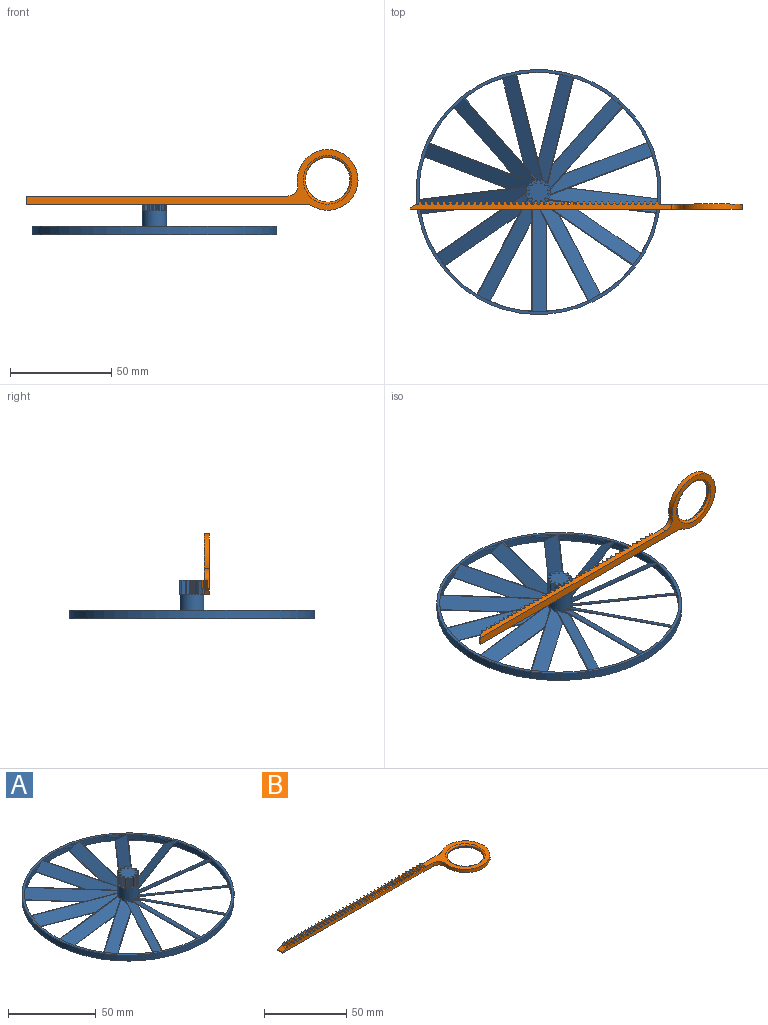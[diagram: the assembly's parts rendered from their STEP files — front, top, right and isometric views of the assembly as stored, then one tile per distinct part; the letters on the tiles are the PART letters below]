
ASSEMBLY  parts=2 mates=1
PART A: 95 faces, bbox 121.1x121.1x19.1 mm
  f0: plane 2.1x1.71mm, normal (0,0,1), area 2.1mm2, adj f12,f59,f62,f93
  f1: plane 1.96x1.96mm, normal (0,0,1), area 2.1mm2, adj f12,f90,f92,f94
  f2: plane 2.1x1.71mm, normal (0,0,1), area 2.1mm2, adj f12,f87,f89,f91
  f3: plane 2.1x1.71mm, normal (0,0,1), area 2.1mm2, adj f12,f84,f86,f88
  f4: plane 1.96x1.96mm, normal (0,0,1), area 2.1mm2, adj f12,f81,f83,f85
  f5: plane 2.1x1.71mm, normal (0,0,1), area 2.1mm2, adj f12,f78,f80,f82
  f6: plane 2.1x1.71mm, normal (0,0,1), area 2.1mm2, adj f12,f75,f77,f79
  f7: plane 1.96x1.96mm, normal (0,0,1), area 2.1mm2, adj f12,f72,f74,f76
  f8: plane 2.1x1.71mm, normal (0,0,1), area 2.1mm2, adj f12,f69,f71,f73
  f9: plane 2.1x1.71mm, normal (0,0,1), area 2.1mm2, adj f12,f66,f68,f70
  f10: plane 1.96x1.96mm, normal (0,0,1), area 2.1mm2, adj f12,f63,f65,f67
  f11: plane 2.1x1.71mm, normal (0,0,1), area 2.1mm2, adj f12,f58,f61,f64
  f12: cylinder r=6mm len=19mm, axis (0,0,-1), area 474.6mm2, adj f0,f1,f2,f3,f4,f5,f6,f7
  f13: cylinder r=6mm len=1.57mm, axis (0,0,-1), area 0.4mm2, adj f12,f16,f36
  f14: cylinder r=6mm len=4.1mm, axis (0,0,-1), area 2.9mm2, adj f12,f16,f37,f38
  f15: cylinder r=6mm len=5.7mm, axis (0,0,-1), area 6.2mm2, adj f12,f16,f39,f40
  f16: plane 121x121mm, normal (0,0,-1), area 885.8mm2, adj f12,f13,f14,f15,f17,f18,f19,f20
  f17: cylinder r=20mm len=54.2mm, axis (0,1,0), area 430.3mm2, adj f12,f16,f43,f57
  f18: plane 54.47x6.93mm, normal (0.5,0,0.87), area 427.4mm2, adj f12,f16,f44,f57
  f19: cylinder r=20mm len=51.21mm, axis (-0.46,0.89,0), area 430.3mm2, adj f12,f16,f44,f57
  f20: plane 50.9x31.41mm, normal (0.44,-0.23,0.87), area 427.4mm2, adj f12,f16,f43,f57
  f21: plane 51.38x31.16mm, normal (0.44,0.23,0.87), area 427.4mm2, adj f12,f16,f45,f57
  f22: cylinder r=20mm len=48.54mm, axis (-0.82,0.57,0), area 430.3mm2, adj f12,f16,f45,f57
  f23: plane 48.25x36.6mm, normal (0.28,0.41,0.87), area 427.4mm2, adj f12,f16,f46,f57
  f24: cylinder r=20mm len=54.64mm, axis (-0.99,0.12,0), area 430.3mm2, adj f12,f16,f46,f57
  f25: plane 54.29x13.43mm, normal (0.06,0.5,0.87), area 427.4mm2, adj f12,f16,f47,f57
  f26: cylinder r=20mm len=53.14mm, axis (-0.94,-0.35,0), area 430.3mm2, adj f12,f16,f47,f57
  f27: plane 53.31x25.57mm, normal (-0.18,0.47,0.87), area 427.4mm2, adj f12,f16,f48,f57
  f28: cylinder r=20mm len=45.16mm, axis (-0.66,-0.75,0), area 430.3mm2, adj f12,f16,f48,f57
  f29: plane 44.9x41.25mm, normal (-0.37,0.33,0.87), area 427.4mm2, adj f12,f16,f49,f57
  f30: cylinder r=20mm len=54.28mm, axis (-0.24,-0.97,0), area 430.3mm2, adj f12,f16,f49,f57
  f31: plane 53.94x19.74mm, normal (-0.49,0.12,0.87), area 427.4mm2, adj f12,f16,f50,f57
  f32: cylinder r=20mm len=54.28mm, axis (0.24,-0.97,0), area 430.3mm2, adj f12,f16,f50,f57
  f33: plane 54.47x19.61mm, normal (-0.49,-0.12,0.87), area 427.4mm2, adj f12,f16,f51,f57
  f34: cylinder r=20mm len=45.16mm, axis (0.66,-0.75,0), area 430.3mm2, adj f12,f16,f51,f57
  f35: plane 45.3x40.9mm, normal (-0.37,-0.33,0.87), area 427.4mm2, adj f12,f16,f52,f57
  f36: cylinder r=20mm len=53.14mm, axis (0.94,-0.35,0), area 430.3mm2, adj f12,f13,f16,f52,f57
  f37: plane 52.9x25.85mm, normal (-0.18,-0.47,0.87), area 427.4mm2, adj f12,f14,f16,f53,f57
  f38: cylinder r=20mm len=54.64mm, axis (0.99,0.12,0), area 430.3mm2, adj f12,f14,f16,f53,f57
  f39: plane 54.87x13.42mm, normal (0.06,-0.5,0.87), area 427.4mm2, adj f12,f15,f16,f54,f57
  f40: cylinder r=20mm len=48.54mm, axis (0.82,0.57,0), area 430.3mm2, adj f15,f16,f54,f57
  f41: plane 48.7x36.29mm, normal (0.28,-0.41,0.87), area 427.4mm2, adj f12,f16,f55,f57
  f42: cylinder r=20mm len=51.21mm, axis (0.46,0.89,0), area 430.3mm2, adj f12,f16,f55,f57
  f43: cylinder r=59.1mm len=33.65mm, axis (0,0,-1), area 110.7mm2, adj f16,f17,f20,f57
  f44: cylinder r=59.1mm len=33.6mm, axis (0,0,-1), area 110.7mm2, adj f16,f18,f19,f57
  f45: cylinder r=59.1mm len=25.85mm, axis (0,0,-1), area 110.7mm2, adj f16,f21,f22,f57
  f46: cylinder r=59.1mm len=32.42mm, axis (0,0,-1), area 110.7mm2, adj f16,f23,f24,f57
  f47: cylinder r=59.1mm len=34.37mm, axis (0,0,-1), area 110.7mm2, adj f16,f25,f26,f57
  f48: cylinder r=59.1mm len=28.44mm, axis (0,0,-1), area 110.7mm2, adj f16,f27,f28,f57
  f49: cylinder r=59.1mm len=30.71mm, axis (0,0,-1), area 110.7mm2, adj f16,f29,f30,f57
  f50: cylinder r=59.1mm len=34.63mm, axis (0,0,-1), area 110.7mm2, adj f16,f31,f32,f57
  f51: cylinder r=59.1mm len=30.62mm, axis (0,0,-1), area 110.7mm2, adj f16,f33,f34,f57
  f52: cylinder r=59.1mm len=28.56mm, axis (0,0,-1), area 110.7mm2, adj f16,f35,f36,f57
  f53: cylinder r=59.1mm len=34.39mm, axis (0,0,-1), area 110.7mm2, adj f16,f37,f38,f57
  f54: cylinder r=59.1mm len=32.34mm, axis (0,0,-1), area 110.7mm2, adj f16,f39,f40,f57
  f55: cylinder r=59.1mm len=25.99mm, axis (0,0,-1), area 110.7mm2, adj f16,f41,f42,f57
  f56: cylinder r=60.5mm len=121mm, axis (0,0,-1), area 1520.5mm2, adj f16,f57
  f57: plane 121x121mm, normal (0,0,1), area 771.7mm2, adj f12,f17,f18,f19,f20,f21,f22,f23
  f58: plane 7x1.57mm, normal (-0.97,0.26,0), area 11.4mm2, adj f11,f12,f60,f61
  f59: plane 7x1.57mm, normal (0.97,0.26,0), area 11.4mm2, adj f0,f12,f60,f62
  f60: plane 12x12mm, normal (0,0,1), area 88.4mm2, adj f12,f58,f59,f61,f62,f63,f64,f65
  f61: cylinder r=4.5mm len=7mm, axis (0,0,-1), area 3.8mm2, adj f11,f58,f60,f64
  f62: cylinder r=4.5mm len=7mm, axis (0,0,-1), area 3.8mm2, adj f0,f59,f60,f93
  f63: plane 7x1.57mm, normal (-0.97,-0.26,0), area 11.4mm2, adj f10,f12,f60,f65
  f64: plane 7x1.15mm, normal (0.71,0.71,0), area 11.4mm2, adj f11,f12,f60,f61
  f65: cylinder r=4.5mm len=7mm, axis (0,0,-1), area 3.8mm2, adj f10,f60,f63,f67
  f66: plane 7x1.15mm, normal (-0.71,-0.71,0), area 11.4mm2, adj f9,f12,f60,f68
  f67: plane 7x1.57mm, normal (0.26,0.97,0), area 11.4mm2, adj f10,f12,f60,f65
  f68: cylinder r=4.5mm len=7mm, axis (0,0,-1), area 3.8mm2, adj f9,f60,f66,f70
  f69: plane 7x1.57mm, normal (-0.26,-0.97,0), area 11.4mm2, adj f8,f12,f60,f71
  f70: plane 7x1.57mm, normal (-0.26,0.97,0), area 11.4mm2, adj f9,f12,f60,f68
  f71: cylinder r=4.5mm len=7mm, axis (0,0,-1), area 3.8mm2, adj f8,f60,f69,f73
  f72: plane 7x1.57mm, normal (0.26,-0.97,0), area 11.4mm2, adj f7,f12,f60,f74
  f73: plane 7x1.15mm, normal (-0.71,0.71,0), area 11.4mm2, adj f8,f12,f60,f71
  f74: cylinder r=4.5mm len=7mm, axis (0,0,-1), area 3.8mm2, adj f7,f60,f72,f76
  f75: plane 7x1.15mm, normal (0.71,-0.71,0), area 11.4mm2, adj f6,f12,f60,f77
  f76: plane 7x1.57mm, normal (-0.97,0.26,0), area 11.4mm2, adj f7,f12,f60,f74
  f77: cylinder r=4.5mm len=7mm, axis (0,0,-1), area 3.8mm2, adj f6,f60,f75,f79
  f78: plane 7x1.57mm, normal (0.97,-0.26,0), area 11.4mm2, adj f5,f12,f60,f80
  f79: plane 7x1.57mm, normal (-0.97,-0.26,0), area 11.4mm2, adj f6,f12,f60,f77
  f80: cylinder r=4.5mm len=7mm, axis (0,0,-1), area 3.8mm2, adj f5,f60,f78,f82
  f81: plane 7x1.57mm, normal (0.97,0.26,0), area 11.4mm2, adj f4,f12,f60,f83
  f82: plane 7x1.15mm, normal (-0.71,-0.71,0), area 11.4mm2, adj f5,f12,f60,f80
  f83: cylinder r=4.5mm len=7mm, axis (0,0,-1), area 3.8mm2, adj f4,f60,f81,f85
  f84: plane 7x1.15mm, normal (0.71,0.71,0), area 11.4mm2, adj f3,f12,f60,f86
  f85: plane 7x1.57mm, normal (-0.26,-0.97,0), area 11.4mm2, adj f4,f12,f60,f83
  f86: cylinder r=4.5mm len=7mm, axis (0,0,-1), area 3.8mm2, adj f3,f60,f84,f88
  f87: plane 7x1.57mm, normal (0.26,0.97,0), area 11.4mm2, adj f2,f12,f60,f89
  f88: plane 7x1.57mm, normal (0.26,-0.97,0), area 11.4mm2, adj f3,f12,f60,f86
  f89: cylinder r=4.5mm len=7mm, axis (0,0,-1), area 3.8mm2, adj f2,f60,f87,f91
  f90: plane 7x1.57mm, normal (-0.26,0.97,0), area 11.4mm2, adj f1,f12,f60,f92
  f91: plane 7x1.15mm, normal (0.71,-0.71,0), area 11.4mm2, adj f2,f12,f60,f89
  f92: cylinder r=4.5mm len=7mm, axis (0,0,-1), area 3.8mm2, adj f1,f60,f90,f94
  f93: plane 7x1.15mm, normal (-0.71,0.71,0), area 11.4mm2, adj f0,f12,f60,f62
  f94: plane 7x1.57mm, normal (0.97,-0.26,0), area 11.4mm2, adj f1,f12,f60,f92
PART B: 252 faces, bbox 164x30x3.8 mm
  f0: plane 4x0.94mm, normal (-0.87,0,0.49), area 4.3mm2, adj f1,f6,f7,f8
  f1: plane 4x0.38mm, normal (-0.81,0,0.59), area 1.9mm2, adj f0,f7,f8,f243
  f2: plane 164.01x30mm, normal (0,0,-1), area 816.3mm2, adj f7,f8,f245,f246,f248,f250,f251
  f3: plane 4x1mm, normal (0,0,1), area 4mm2, adj f4,f7,f8,f10
  f4: plane 4x0.38mm, normal (0.81,0,0.59), area 1.9mm2, adj f3,f5,f7,f8
  f5: plane 4x0.94mm, normal (0.87,0,0.49), area 4.3mm2, adj f4,f6,f7,f8
  f6: plane 4x0.4mm, normal (0,0,1), area 1.6mm2, adj f0,f5,f7,f8
  f7: plane 129.23x3.82mm, normal (0,-1,0), area 380.9mm2, adj f0,f1,f2,f3,f4,f5,f6,f9
  f8: plane 138.47x3.82mm, normal (0,1,0), area 404mm2, adj f0,f1,f2,f3,f4,f5,f6,f9
  f9: plane 4x0.94mm, normal (-0.87,0,0.49), area 4.3mm2, adj f7,f8,f10,f14
  f10: plane 4x0.38mm, normal (-0.81,0,0.59), area 1.9mm2, adj f3,f7,f8,f9
  f11: plane 4x1mm, normal (0,0,1), area 4mm2, adj f7,f8,f12,f16
  f12: plane 4x0.38mm, normal (0.81,0,0.59), area 1.9mm2, adj f7,f8,f11,f13
  f13: plane 4x0.94mm, normal (0.87,0,0.49), area 4.3mm2, adj f7,f8,f12,f14
  f14: plane 4x0.4mm, normal (0,0,1), area 1.6mm2, adj f7,f8,f9,f13
  f15: plane 4x0.94mm, normal (-0.87,0,0.49), area 4.3mm2, adj f7,f8,f16,f20
  f16: plane 4x0.38mm, normal (-0.81,0,0.59), area 1.9mm2, adj f7,f8,f11,f15
  f17: plane 4x1mm, normal (0,0,1), area 4mm2, adj f7,f8,f18,f22
  f18: plane 4x0.38mm, normal (0.81,0,0.59), area 1.9mm2, adj f7,f8,f17,f19
  f19: plane 4x0.94mm, normal (0.87,0,0.49), area 4.3mm2, adj f7,f8,f18,f20
  f20: plane 4x0.4mm, normal (0,0,1), area 1.6mm2, adj f7,f8,f15,f19
  f21: plane 4x0.94mm, normal (-0.87,0,0.49), area 4.3mm2, adj f7,f8,f22,f26
  f22: plane 4x0.38mm, normal (-0.81,0,0.59), area 1.9mm2, adj f7,f8,f17,f21
  f23: plane 4x1mm, normal (0,0,1), area 4mm2, adj f7,f8,f24,f28
  f24: plane 4x0.38mm, normal (0.81,0,0.59), area 1.9mm2, adj f7,f8,f23,f25
  f25: plane 4x0.94mm, normal (0.87,0,0.49), area 4.3mm2, adj f7,f8,f24,f26
  f26: plane 4x0.4mm, normal (0,0,1), area 1.6mm2, adj f7,f8,f21,f25
  f27: plane 4x0.94mm, normal (-0.87,0,0.49), area 4.3mm2, adj f7,f8,f28,f32
  f28: plane 4x0.38mm, normal (-0.81,0,0.59), area 1.9mm2, adj f7,f8,f23,f27
  f29: plane 4x1mm, normal (0,0,1), area 4mm2, adj f7,f8,f30,f34
  f30: plane 4x0.38mm, normal (0.81,0,0.59), area 1.9mm2, adj f7,f8,f29,f31
  f31: plane 4x0.94mm, normal (0.87,0,0.49), area 4.3mm2, adj f7,f8,f30,f32
  f32: plane 4x0.4mm, normal (0,0,1), area 1.6mm2, adj f7,f8,f27,f31
  f33: plane 4x0.94mm, normal (-0.87,0,0.49), area 4.3mm2, adj f7,f8,f34,f38
  f34: plane 4x0.38mm, normal (-0.81,0,0.59), area 1.9mm2, adj f7,f8,f29,f33
  f35: plane 4x1mm, normal (0,0,1), area 4mm2, adj f7,f8,f36,f40
  f36: plane 4x0.38mm, normal (0.81,0,0.59), area 1.9mm2, adj f7,f8,f35,f37
  f37: plane 4x0.94mm, normal (0.87,0,0.49), area 4.3mm2, adj f7,f8,f36,f38
  f38: plane 4x0.4mm, normal (0,0,1), area 1.6mm2, adj f7,f8,f33,f37
  f39: plane 4x0.94mm, normal (-0.87,0,0.49), area 4.3mm2, adj f7,f8,f40,f44
  f40: plane 4x0.38mm, normal (-0.81,0,0.59), area 1.9mm2, adj f7,f8,f35,f39
  f41: plane 4x1mm, normal (0,0,1), area 4mm2, adj f7,f8,f42,f46
  f42: plane 4x0.38mm, normal (0.81,0,0.59), area 1.9mm2, adj f7,f8,f41,f43
  f43: plane 4x0.94mm, normal (0.87,0,0.49), area 4.3mm2, adj f7,f8,f42,f44
  f44: plane 4x0.4mm, normal (0,0,1), area 1.6mm2, adj f7,f8,f39,f43
  f45: plane 4x0.94mm, normal (-0.87,0,0.49), area 4.3mm2, adj f7,f8,f46,f50
  f46: plane 4x0.38mm, normal (-0.81,0,0.59), area 1.9mm2, adj f7,f8,f41,f45
  f47: plane 4x1mm, normal (0,0,1), area 4mm2, adj f7,f8,f48,f52
  f48: plane 4x0.38mm, normal (0.81,0,0.59), area 1.9mm2, adj f7,f8,f47,f49
  f49: plane 4x0.94mm, normal (0.87,0,0.49), area 4.3mm2, adj f7,f8,f48,f50
  f50: plane 4x0.4mm, normal (0,0,1), area 1.6mm2, adj f7,f8,f45,f49
  f51: plane 4x0.94mm, normal (-0.87,0,0.49), area 4.3mm2, adj f7,f8,f52,f56
  f52: plane 4x0.38mm, normal (-0.81,0,0.59), area 1.9mm2, adj f7,f8,f47,f51
  f53: plane 4x1mm, normal (0,0,1), area 4mm2, adj f7,f8,f54,f58
  f54: plane 4x0.38mm, normal (0.81,0,0.59), area 1.9mm2, adj f7,f8,f53,f55
  f55: plane 4x0.94mm, normal (0.87,0,0.49), area 4.3mm2, adj f7,f8,f54,f56
  f56: plane 4x0.4mm, normal (0,0,1), area 1.6mm2, adj f7,f8,f51,f55
  f57: plane 4x0.94mm, normal (-0.87,0,0.49), area 4.3mm2, adj f7,f8,f58,f62
  f58: plane 4x0.38mm, normal (-0.81,0,0.59), area 1.9mm2, adj f7,f8,f53,f57
  f59: plane 4x1mm, normal (0,0,1), area 4mm2, adj f7,f8,f60,f64
  f60: plane 4x0.38mm, normal (0.81,0,0.59), area 1.9mm2, adj f7,f8,f59,f61
  f61: plane 4x0.94mm, normal (0.87,0,0.49), area 4.3mm2, adj f7,f8,f60,f62
  f62: plane 4x0.4mm, normal (0,0,1), area 1.6mm2, adj f7,f8,f57,f61
  f63: plane 4x0.94mm, normal (-0.87,0,0.49), area 4.3mm2, adj f7,f8,f64,f68
  f64: plane 4x0.38mm, normal (-0.81,0,0.59), area 1.9mm2, adj f7,f8,f59,f63
  f65: plane 4x1mm, normal (0,0,1), area 4mm2, adj f7,f8,f66,f70
  f66: plane 4x0.38mm, normal (0.81,0,0.59), area 1.9mm2, adj f7,f8,f65,f67
  f67: plane 4x0.94mm, normal (0.87,0,0.49), area 4.3mm2, adj f7,f8,f66,f68
  f68: plane 4x0.4mm, normal (0,0,1), area 1.6mm2, adj f7,f8,f63,f67
  f69: plane 4x0.94mm, normal (-0.87,0,0.49), area 4.3mm2, adj f7,f8,f70,f74
  f70: plane 4x0.38mm, normal (-0.81,0,0.59), area 1.9mm2, adj f7,f8,f65,f69
  f71: plane 4x1mm, normal (0,0,1), area 4mm2, adj f7,f8,f72,f76
  f72: plane 4x0.38mm, normal (0.81,0,0.59), area 1.9mm2, adj f7,f8,f71,f73
  f73: plane 4x0.94mm, normal (0.87,0,0.49), area 4.3mm2, adj f7,f8,f72,f74
  f74: plane 4x0.4mm, normal (0,0,1), area 1.6mm2, adj f7,f8,f69,f73
  f75: plane 4x0.94mm, normal (-0.87,0,0.49), area 4.3mm2, adj f7,f8,f76,f80
  f76: plane 4x0.38mm, normal (-0.81,0,0.59), area 1.9mm2, adj f7,f8,f71,f75
  f77: plane 4x1mm, normal (0,0,1), area 4mm2, adj f7,f8,f78,f82
  f78: plane 4x0.38mm, normal (0.81,0,0.59), area 1.9mm2, adj f7,f8,f77,f79
  f79: plane 4x0.94mm, normal (0.87,0,0.49), area 4.3mm2, adj f7,f8,f78,f80
  f80: plane 4x0.4mm, normal (0,0,1), area 1.6mm2, adj f7,f8,f75,f79
  f81: plane 4x0.94mm, normal (-0.87,0,0.49), area 4.3mm2, adj f7,f8,f82,f86
  f82: plane 4x0.38mm, normal (-0.81,0,0.59), area 1.9mm2, adj f7,f8,f77,f81
  f83: plane 4x1mm, normal (0,0,1), area 4mm2, adj f7,f8,f84,f88
  f84: plane 4x0.38mm, normal (0.81,0,0.59), area 1.9mm2, adj f7,f8,f83,f85
  f85: plane 4x0.94mm, normal (0.87,0,0.49), area 4.3mm2, adj f7,f8,f84,f86
  f86: plane 4x0.4mm, normal (0,0,1), area 1.6mm2, adj f7,f8,f81,f85
  f87: plane 4x0.94mm, normal (-0.87,0,0.49), area 4.3mm2, adj f7,f8,f88,f92
  f88: plane 4x0.38mm, normal (-0.81,0,0.59), area 1.9mm2, adj f7,f8,f83,f87
  f89: plane 4x1mm, normal (0,0,1), area 4mm2, adj f7,f8,f90,f94
  f90: plane 4x0.38mm, normal (0.81,0,0.59), area 1.9mm2, adj f7,f8,f89,f91
  f91: plane 4x0.94mm, normal (0.87,0,0.49), area 4.3mm2, adj f7,f8,f90,f92
  f92: plane 4x0.4mm, normal (0,0,1), area 1.6mm2, adj f7,f8,f87,f91
  f93: plane 4x0.94mm, normal (-0.87,0,0.49), area 4.3mm2, adj f7,f8,f94,f98
  f94: plane 4x0.38mm, normal (-0.81,0,0.59), area 1.9mm2, adj f7,f8,f89,f93
  f95: plane 4x1mm, normal (0,0,1), area 4mm2, adj f7,f8,f96,f100
  f96: plane 4x0.38mm, normal (0.81,0,0.59), area 1.9mm2, adj f7,f8,f95,f97
  f97: plane 4x0.94mm, normal (0.87,0,0.49), area 4.3mm2, adj f7,f8,f96,f98
  f98: plane 4x0.4mm, normal (0,0,1), area 1.6mm2, adj f7,f8,f93,f97
  f99: plane 4x0.94mm, normal (-0.87,0,0.49), area 4.3mm2, adj f7,f8,f100,f104
  f100: plane 4x0.38mm, normal (-0.81,0,0.59), area 1.9mm2, adj f7,f8,f95,f99
  f101: plane 4x1mm, normal (0,0,1), area 4mm2, adj f7,f8,f102,f106
  f102: plane 4x0.38mm, normal (0.81,0,0.59), area 1.9mm2, adj f7,f8,f101,f103
  f103: plane 4x0.94mm, normal (0.87,0,0.49), area 4.3mm2, adj f7,f8,f102,f104
  f104: plane 4x0.4mm, normal (0,0,1), area 1.6mm2, adj f7,f8,f99,f103
  f105: plane 4x0.94mm, normal (-0.87,0,0.49), area 4.3mm2, adj f7,f8,f106,f110
  f106: plane 4x0.38mm, normal (-0.81,0,0.59), area 1.9mm2, adj f7,f8,f101,f105
  f107: plane 4x1mm, normal (0,0,1), area 4mm2, adj f7,f8,f108,f112
  f108: plane 4x0.38mm, normal (0.81,0,0.59), area 1.9mm2, adj f7,f8,f107,f109
  f109: plane 4x0.94mm, normal (0.87,0,0.49), area 4.3mm2, adj f7,f8,f108,f110
  f110: plane 4x0.4mm, normal (0,0,1), area 1.6mm2, adj f7,f8,f105,f109
  f111: plane 4x0.94mm, normal (-0.87,0,0.49), area 4.3mm2, adj f7,f8,f112,f116
  f112: plane 4x0.38mm, normal (-0.81,0,0.59), area 1.9mm2, adj f7,f8,f107,f111
  f113: plane 4x1mm, normal (0,0,1), area 4mm2, adj f7,f8,f114,f118
  f114: plane 4x0.38mm, normal (0.81,0,0.59), area 1.9mm2, adj f7,f8,f113,f115
  f115: plane 4x0.94mm, normal (0.87,0,0.49), area 4.3mm2, adj f7,f8,f114,f116
  f116: plane 4x0.4mm, normal (0,0,1), area 1.6mm2, adj f7,f8,f111,f115
  f117: plane 4x0.94mm, normal (-0.87,0,0.49), area 4.3mm2, adj f7,f8,f118,f122
  f118: plane 4x0.38mm, normal (-0.81,0,0.59), area 1.9mm2, adj f7,f8,f113,f117
  f119: plane 4x1mm, normal (0,0,1), area 4mm2, adj f7,f8,f120,f124
  f120: plane 4x0.38mm, normal (0.81,0,0.59), area 1.9mm2, adj f7,f8,f119,f121
  f121: plane 4x0.94mm, normal (0.87,0,0.49), area 4.3mm2, adj f7,f8,f120,f122
  f122: plane 4x0.4mm, normal (0,0,1), area 1.6mm2, adj f7,f8,f117,f121
  f123: plane 4x0.94mm, normal (-0.87,0,0.49), area 4.3mm2, adj f7,f8,f124,f128
  f124: plane 4x0.38mm, normal (-0.81,0,0.59), area 1.9mm2, adj f7,f8,f119,f123
  f125: plane 4x1mm, normal (0,0,1), area 4mm2, adj f7,f8,f126,f130
  f126: plane 4x0.38mm, normal (0.81,0,0.59), area 1.9mm2, adj f7,f8,f125,f127
  f127: plane 4x0.94mm, normal (0.87,0,0.49), area 4.3mm2, adj f7,f8,f126,f128
  f128: plane 4x0.4mm, normal (0,0,1), area 1.6mm2, adj f7,f8,f123,f127
  f129: plane 4x0.94mm, normal (-0.87,0,0.49), area 4.3mm2, adj f7,f8,f130,f134
  f130: plane 4x0.38mm, normal (-0.81,0,0.59), area 1.9mm2, adj f7,f8,f125,f129
  f131: plane 4x1mm, normal (0,0,1), area 4mm2, adj f7,f8,f132,f136
  f132: plane 4x0.38mm, normal (0.81,0,0.59), area 1.9mm2, adj f7,f8,f131,f133
  f133: plane 4x0.94mm, normal (0.87,0,0.49), area 4.3mm2, adj f7,f8,f132,f134
  f134: plane 4x0.4mm, normal (0,0,1), area 1.6mm2, adj f7,f8,f129,f133
  f135: plane 4x0.94mm, normal (-0.87,0,0.49), area 4.3mm2, adj f7,f8,f136,f140
  f136: plane 4x0.38mm, normal (-0.81,0,0.59), area 1.9mm2, adj f7,f8,f131,f135
  f137: plane 4x1mm, normal (0,0,1), area 4mm2, adj f7,f8,f138,f142
  f138: plane 4x0.38mm, normal (0.81,0,0.59), area 1.9mm2, adj f7,f8,f137,f139
  f139: plane 4x0.94mm, normal (0.87,0,0.49), area 4.3mm2, adj f7,f8,f138,f140
  f140: plane 4x0.4mm, normal (0,0,1), area 1.6mm2, adj f7,f8,f135,f139
  f141: plane 4x0.94mm, normal (-0.87,0,0.49), area 4.3mm2, adj f7,f8,f142,f146
  f142: plane 4x0.38mm, normal (-0.81,0,0.59), area 1.9mm2, adj f7,f8,f137,f141
  f143: plane 4x1mm, normal (0,0,1), area 4mm2, adj f7,f8,f144,f148
  f144: plane 4x0.38mm, normal (0.81,0,0.59), area 1.9mm2, adj f7,f8,f143,f145
  f145: plane 4x0.94mm, normal (0.87,0,0.49), area 4.3mm2, adj f7,f8,f144,f146
  f146: plane 4x0.4mm, normal (0,0,1), area 1.6mm2, adj f7,f8,f141,f145
  f147: plane 4x0.94mm, normal (-0.87,0,0.49), area 4.3mm2, adj f7,f8,f148,f152
  f148: plane 4x0.38mm, normal (-0.81,0,0.59), area 1.9mm2, adj f7,f8,f143,f147
  f149: plane 4x1mm, normal (0,0,1), area 4mm2, adj f7,f8,f150,f154
  f150: plane 4x0.38mm, normal (0.81,0,0.59), area 1.9mm2, adj f7,f8,f149,f151
  f151: plane 4x0.94mm, normal (0.87,0,0.49), area 4.3mm2, adj f7,f8,f150,f152
  f152: plane 4x0.4mm, normal (0,0,1), area 1.6mm2, adj f7,f8,f147,f151
  f153: plane 4x0.94mm, normal (-0.87,0,0.49), area 4.3mm2, adj f7,f8,f154,f158
  f154: plane 4x0.38mm, normal (-0.81,0,0.59), area 1.9mm2, adj f7,f8,f149,f153
  f155: plane 4x1mm, normal (0,0,1), area 4mm2, adj f7,f8,f156,f160
  f156: plane 4x0.38mm, normal (0.81,0,0.59), area 1.9mm2, adj f7,f8,f155,f157
  f157: plane 4x0.94mm, normal (0.87,0,0.49), area 4.3mm2, adj f7,f8,f156,f158
  f158: plane 4x0.4mm, normal (0,0,1), area 1.6mm2, adj f7,f8,f153,f157
  f159: plane 4x0.94mm, normal (-0.87,0,0.49), area 4.3mm2, adj f7,f8,f160,f164
  f160: plane 4x0.38mm, normal (-0.81,0,0.59), area 1.9mm2, adj f7,f8,f155,f159
  f161: plane 4x1mm, normal (0,0,1), area 4mm2, adj f7,f8,f162,f166
  f162: plane 4x0.38mm, normal (0.81,0,0.59), area 1.9mm2, adj f7,f8,f161,f163
  f163: plane 4x0.94mm, normal (0.87,0,0.49), area 4.3mm2, adj f7,f8,f162,f164
  f164: plane 4x0.4mm, normal (0,0,1), area 1.6mm2, adj f7,f8,f159,f163
  f165: plane 4x0.94mm, normal (-0.87,0,0.49), area 4.3mm2, adj f7,f8,f166,f170
  f166: plane 4x0.38mm, normal (-0.81,0,0.59), area 1.9mm2, adj f7,f8,f161,f165
  f167: plane 4x1mm, normal (0,0,1), area 4mm2, adj f7,f8,f168,f172
  f168: plane 4x0.38mm, normal (0.81,0,0.59), area 1.9mm2, adj f7,f8,f167,f169
  f169: plane 4x0.94mm, normal (0.87,0,0.49), area 4.3mm2, adj f7,f8,f168,f170
  f170: plane 4x0.4mm, normal (0,0,1), area 1.6mm2, adj f7,f8,f165,f169
  f171: plane 4x0.94mm, normal (-0.87,0,0.49), area 4.3mm2, adj f7,f8,f172,f176
  f172: plane 4x0.38mm, normal (-0.81,0,0.59), area 1.9mm2, adj f7,f8,f167,f171
  f173: plane 4x1mm, normal (0,0,1), area 4mm2, adj f7,f8,f174,f178
  f174: plane 4x0.38mm, normal (0.81,0,0.59), area 1.9mm2, adj f7,f8,f173,f175
  f175: plane 4x0.94mm, normal (0.87,0,0.49), area 4.3mm2, adj f7,f8,f174,f176
  f176: plane 4x0.4mm, normal (0,0,1), area 1.6mm2, adj f7,f8,f171,f175
  f177: plane 4x0.94mm, normal (-0.87,0,0.49), area 4.3mm2, adj f7,f8,f178,f182
  f178: plane 4x0.38mm, normal (-0.81,0,0.59), area 1.9mm2, adj f7,f8,f173,f177
  f179: plane 4x1mm, normal (0,0,1), area 4mm2, adj f7,f8,f180,f184
  f180: plane 4x0.38mm, normal (0.81,0,0.59), area 1.9mm2, adj f7,f8,f179,f181
  f181: plane 4x0.94mm, normal (0.87,0,0.49), area 4.3mm2, adj f7,f8,f180,f182
  f182: plane 4x0.4mm, normal (0,0,1), area 1.6mm2, adj f7,f8,f177,f181
  f183: plane 4x0.94mm, normal (-0.87,0,0.49), area 4.3mm2, adj f7,f8,f184,f188
  f184: plane 4x0.38mm, normal (-0.81,0,0.59), area 1.9mm2, adj f7,f8,f179,f183
  f185: plane 4x1mm, normal (0,0,1), area 4mm2, adj f7,f8,f186,f190
  f186: plane 4x0.38mm, normal (0.81,0,0.59), area 1.9mm2, adj f7,f8,f185,f187
  f187: plane 4x0.94mm, normal (0.87,0,0.49), area 4.3mm2, adj f7,f8,f186,f188
  f188: plane 4x0.4mm, normal (0,0,1), area 1.6mm2, adj f7,f8,f183,f187
  f189: plane 4x0.94mm, normal (-0.87,0,0.49), area 4.3mm2, adj f7,f8,f190,f194
  f190: plane 4x0.38mm, normal (-0.81,0,0.59), area 1.9mm2, adj f7,f8,f185,f189
  f191: plane 4x1mm, normal (0,0,1), area 4mm2, adj f7,f8,f192,f196
  f192: plane 4x0.38mm, normal (0.81,0,0.59), area 1.9mm2, adj f7,f8,f191,f193
  f193: plane 4x0.94mm, normal (0.87,0,0.49), area 4.3mm2, adj f7,f8,f192,f194
  f194: plane 4x0.4mm, normal (0,0,1), area 1.6mm2, adj f7,f8,f189,f193
  f195: plane 4x0.94mm, normal (-0.87,0,0.49), area 4.3mm2, adj f7,f8,f196,f200
  f196: plane 4x0.38mm, normal (-0.81,0,0.59), area 1.9mm2, adj f7,f8,f191,f195
  f197: plane 4x1mm, normal (0,0,1), area 4mm2, adj f7,f8,f198,f202
  f198: plane 4x0.38mm, normal (0.81,0,0.59), area 1.9mm2, adj f7,f8,f197,f199
  f199: plane 4x0.94mm, normal (0.87,0,0.49), area 4.3mm2, adj f7,f8,f198,f200
  f200: plane 4x0.4mm, normal (0,0,1), area 1.6mm2, adj f7,f8,f195,f199
  f201: plane 4x0.94mm, normal (-0.87,0,0.49), area 4.3mm2, adj f7,f8,f202,f206
  f202: plane 4x0.38mm, normal (-0.81,0,0.59), area 1.9mm2, adj f7,f8,f197,f201
  f203: plane 4x1mm, normal (0,0,1), area 4mm2, adj f7,f8,f204,f208
  f204: plane 4x0.38mm, normal (0.81,0,0.59), area 1.9mm2, adj f7,f8,f203,f205
  f205: plane 4x0.94mm, normal (0.87,0,0.49), area 4.3mm2, adj f7,f8,f204,f206
  f206: plane 4x0.4mm, normal (0,0,1), area 1.6mm2, adj f7,f8,f201,f205
  f207: plane 4x0.94mm, normal (-0.87,0,0.49), area 4.3mm2, adj f7,f8,f208,f212
  f208: plane 4x0.38mm, normal (-0.81,0,0.59), area 1.9mm2, adj f7,f8,f203,f207
  f209: plane 4x1mm, normal (0,0,1), area 4mm2, adj f7,f8,f210,f214
  f210: plane 4x0.38mm, normal (0.81,0,0.59), area 1.9mm2, adj f7,f8,f209,f211
  f211: plane 4x0.94mm, normal (0.87,0,0.49), area 4.3mm2, adj f7,f8,f210,f212
  f212: plane 4x0.4mm, normal (0,0,1), area 1.6mm2, adj f7,f8,f207,f211
  f213: plane 4x0.94mm, normal (-0.87,0,0.49), area 4.3mm2, adj f7,f8,f214,f218
  f214: plane 4x0.38mm, normal (-0.81,0,0.59), area 1.9mm2, adj f7,f8,f209,f213
  f215: plane 4x1mm, normal (0,0,1), area 4mm2, adj f7,f8,f216,f220
  f216: plane 4x0.38mm, normal (0.81,0,0.59), area 1.9mm2, adj f7,f8,f215,f217
  f217: plane 4x0.94mm, normal (0.87,0,0.49), area 4.3mm2, adj f7,f8,f216,f218
  f218: plane 4x0.4mm, normal (0,0,1), area 1.6mm2, adj f7,f8,f213,f217
  f219: plane 4x0.94mm, normal (-0.87,0,0.49), area 4.3mm2, adj f7,f8,f220,f224
  f220: plane 4x0.38mm, normal (-0.81,0,0.59), area 1.9mm2, adj f7,f8,f215,f219
  f221: plane 4x1mm, normal (0,0,1), area 4mm2, adj f7,f8,f222,f226
  f222: plane 4x0.38mm, normal (0.81,0,0.59), area 1.9mm2, adj f7,f8,f221,f223
  f223: plane 4x0.94mm, normal (0.87,0,0.49), area 4.3mm2, adj f7,f8,f222,f224
  f224: plane 4x0.4mm, normal (0,0,1), area 1.6mm2, adj f7,f8,f219,f223
  f225: plane 4x0.94mm, normal (-0.87,0,0.49), area 4.3mm2, adj f7,f8,f226,f230
  f226: plane 4x0.38mm, normal (-0.81,0,0.59), area 1.9mm2, adj f7,f8,f221,f225
  f227: plane 4x1mm, normal (0,0,1), area 4mm2, adj f7,f8,f228,f232
  f228: plane 4x0.38mm, normal (0.81,0,0.59), area 1.9mm2, adj f7,f8,f227,f229
  f229: plane 4x0.94mm, normal (0.87,0,0.49), area 4.3mm2, adj f7,f8,f228,f230
  f230: plane 4x0.4mm, normal (0,0,1), area 1.6mm2, adj f7,f8,f225,f229
  f231: plane 4x0.94mm, normal (-0.87,0,0.49), area 4.3mm2, adj f7,f8,f232,f236
  f232: plane 4x0.38mm, normal (-0.81,0,0.59), area 1.9mm2, adj f7,f8,f227,f231
  f233: plane 4x1mm, normal (0,0,1), area 4mm2, adj f7,f8,f234,f238
  f234: plane 4x0.38mm, normal (0.81,0,0.59), area 1.9mm2, adj f7,f8,f233,f235
  f235: plane 4x0.94mm, normal (0.87,0,0.49), area 4.3mm2, adj f7,f8,f234,f236
  f236: plane 4x0.4mm, normal (0,0,1), area 1.6mm2, adj f7,f8,f231,f235
  f237: plane 4x0.94mm, normal (-0.87,0,0.49), area 4.3mm2, adj f7,f8,f238,f242
  f238: plane 4x0.38mm, normal (-0.81,0,0.59), area 1.9mm2, adj f7,f8,f233,f237
  f239: plane 41x30mm, normal (0,0,1), area 324.3mm2, adj f7,f8,f240,f246,f249,f250,f251
  f240: plane 4x0.38mm, normal (0.81,0,0.59), area 1.9mm2, adj f7,f8,f239,f241
  f241: plane 4x0.94mm, normal (0.87,0,0.49), area 4.3mm2, adj f7,f8,f240,f242
  f242: plane 4x0.4mm, normal (0,0,1), area 1.6mm2, adj f7,f8,f237,f241
  f243: plane 4x1.01mm, normal (0,0,1), area 4mm2, adj f1,f7,f8,f244
  f244: plane 4x3mm, normal (-0.54,0,0.84), area 14.2mm2, adj f7,f8,f243,f245
  f245: plane 4x0.6mm, normal (-1,0,0), area 2.4mm2, adj f2,f7,f8,f244
  f246: cylinder r=15mm len=30mm, axis (0,0,1), area 203.2mm2, adj f2,f239,f250,f251
  f247: cylinder r=11mm len=22mm, axis (0,0,1), area 34.6mm2, adj f248,f249
  f248: torus R=12mm, axis (0,0,-1), area 112.2mm2, adj f2,f247
  f249: torus R=12mm, axis (0,0,1), area 112.2mm2, adj f239,f247
  f250: cylinder r=5mm len=2.63mm, axis (0,0,1), area 6.9mm2, adj f2,f8,f239,f246
  f251: cylinder r=5mm len=5.75mm, axis (0,0,1), area 21.5mm2, adj f2,f7,f239,f246
PLACE A t=(-19.68,-9.2,-0.35)mm
PLACE B rot(axis=(-1,0,0),90deg) t=(-76.15,-17.7,14.65)mm
MATE planar A.f12 <-> B.f7  axis (0,0,1) through (-19.68,-9.2,18.65)mm
